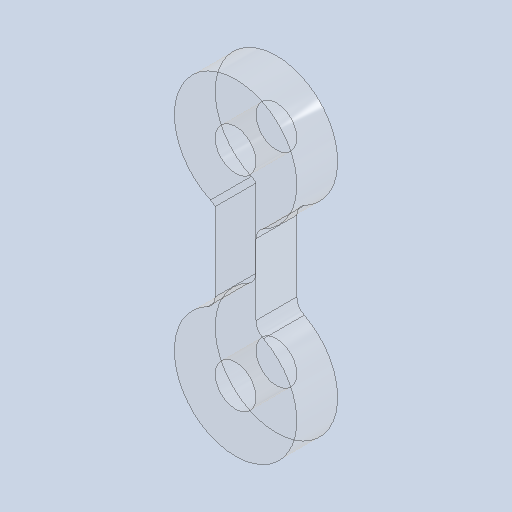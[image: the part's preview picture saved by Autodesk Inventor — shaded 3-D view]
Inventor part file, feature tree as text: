
AUTODESK INVENTOR PART (.ipt)
format: ipt  version: 2023 (Build 270158030, 158C)  size: 128,512 bytes
history: native  units: mm
features: other x1, extrude x1, sketch x1
ambient origin geometry x8: Origin, YZ Plane, XZ Plane, XY Plane, X Axis, Y Axis, Z Axis, Center Point
bodies: Body1 (feature_tree)
feature tree (3):
  other  "ソリッド1"
  extrude  "押し出し1"  Depth=3.0mm TaperAngle=0.0deg
  sketch  "スケッチ1"
